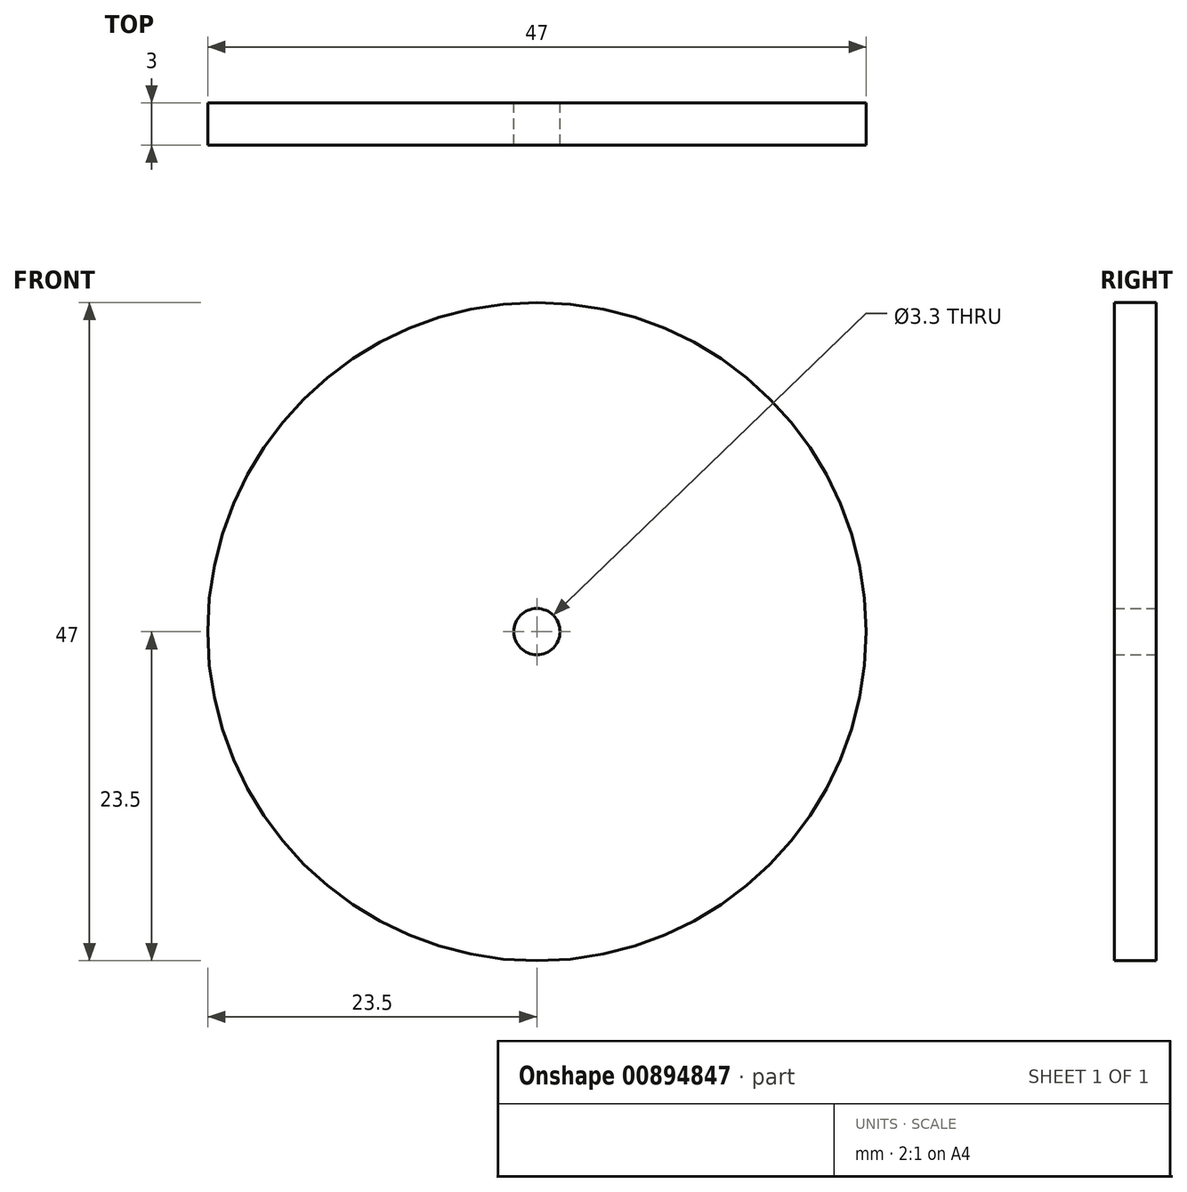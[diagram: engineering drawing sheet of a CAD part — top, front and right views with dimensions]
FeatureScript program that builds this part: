
annotation { "Feature Type Name" : "Feature", "Feature Type Description" : "" }
export const myFeature = defineFeature(function(context is Context, id is Id, definition is map)
    precondition{}
    {
        {
            var Q0;
            Q0=qCreatedBy(makeId("Front.planeOp"),FACE);
            var sketch = newSketch(context, id + "F0", { "sketchPlane" : qUnion([Q0])});
            skCircle(sketch, "E0", {"center": v(0, 0) * mm, "radius": 1.65 * mm});
            skCircle(sketch, "E1", {"center": v(0, 0) * mm, "radius": 23.5 * mm});
            skSolve(sketch);
        }
        {
            var Q0;
            Q0=makeQuery(id+"F0.imprint","IMPRINT",FACE,{"disambiguationData":[TD([[makeQuery(id+"F0.imprint","IMPRINT",EDGE,{"derivedFrom":sQuery(id+"F0.wireOp",EDGE,"E0")}),-1.0]])]});
            extrude(context, id + "F1", {"entities" : qUnion([Q0]), "depth" : 3 * mm, "offsetDistance" : 25 * mm});
        }
    });
